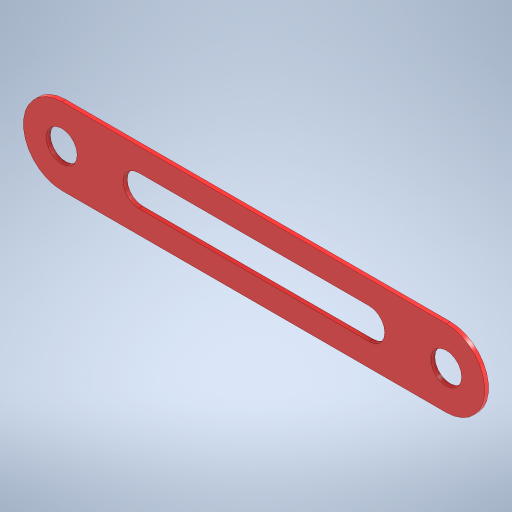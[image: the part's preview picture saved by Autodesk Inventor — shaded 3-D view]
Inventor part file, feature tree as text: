
AUTODESK INVENTOR PART (.ipt)
format: ipt  version: 2024 (Build 280153000, 153)  size: 262,144 bytes
history: native  units: mm
features: extrude x3, sketch x3, other x1, pattern_linear x1
ambient origin geometry x8: Origin, YZ Plane, XZ Plane, XY Plane, X Axis, Y Axis, Z Axis, Center Point
bodies: Body1 (feature_tree)
feature tree (8):
  other  "Těleso1"
  extrude  "Vysunutí1"  Depth=30.0mm
  extrude  "Vysunutí2"  Depth=5.0mm
  pattern_linear  "Obdélníkové pole1"  Spacing1=0.5mm  [1 undecoded]
  extrude  "Vysunutí3"  Depth=4.0mm
  sketch  "Náčrt1"
  sketch  "Náčrt2"
  sketch  "Náčrt3"
note: 1 required parameter value undecoded (feature->parameter linkage not recoverable at this tier; creation-order binding heuristic only, values carry confidence <= 0.55)
